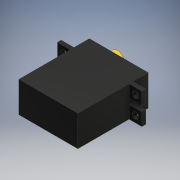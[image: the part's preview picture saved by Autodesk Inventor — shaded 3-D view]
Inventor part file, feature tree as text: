
AUTODESK INVENTOR PART (.ipt)
format: ipt  version: 2018 (Build 220112000, 112)  size: 186,880 bytes
history: native  units: mm
features: extrude x6, sketch x6, other x1
ambient origin geometry x8: Origin, YZ Plane, XZ Plane, XY Plane, X Axis, Y Axis, Z Axis, Center Point
bodies: Body1 (feature_tree)
feature tree (13):
  other  "Sólido1"
  extrude  "Extrusión1"  Depth=12.0mm
  extrude  "Extrusión2"  Depth=27.5mm
  extrude  "Extrusión3"  Depth=5.0mm
  extrude  "Extrusión4"  Depth=5.0mm
  extrude  "Extrusión5"  Depth=7.5mm
  extrude  "Extrusión6"  Depth=5.0mm
  sketch  "Boceto1"  dims[d0=23.0mm d1=12.0mm]
  sketch  "Boceto2"  dims[d2=27.5mm d3=0.0mm d4=17.0mm]
  sketch  "Boceto3"  dims[d5=8.5mm d6=5.0mm]
  sketch  "Boceto4"  dims[d7=5.0mm d8=0.0mm d9=8.5mm]
  sketch  "Boceto5"  dims[d10=1.5mm d11=0.0mm d12=7.5mm]
  sketch  "Boceto6"  dims[d13=1.5mm d14=5.0mm d15=5.0mm d16=5.0mm d17=28.0mm d18=0.0mm d19=0.0mm d20=2.5mm d21=2.5mm d22=2.5mm d23=2.5mm d24=5.0mm d25=0.0mm d26=10.5mm d27=3.0mm d28=4.5mm d29=6.0mm d30=5.0mm d31=0.0mm]
